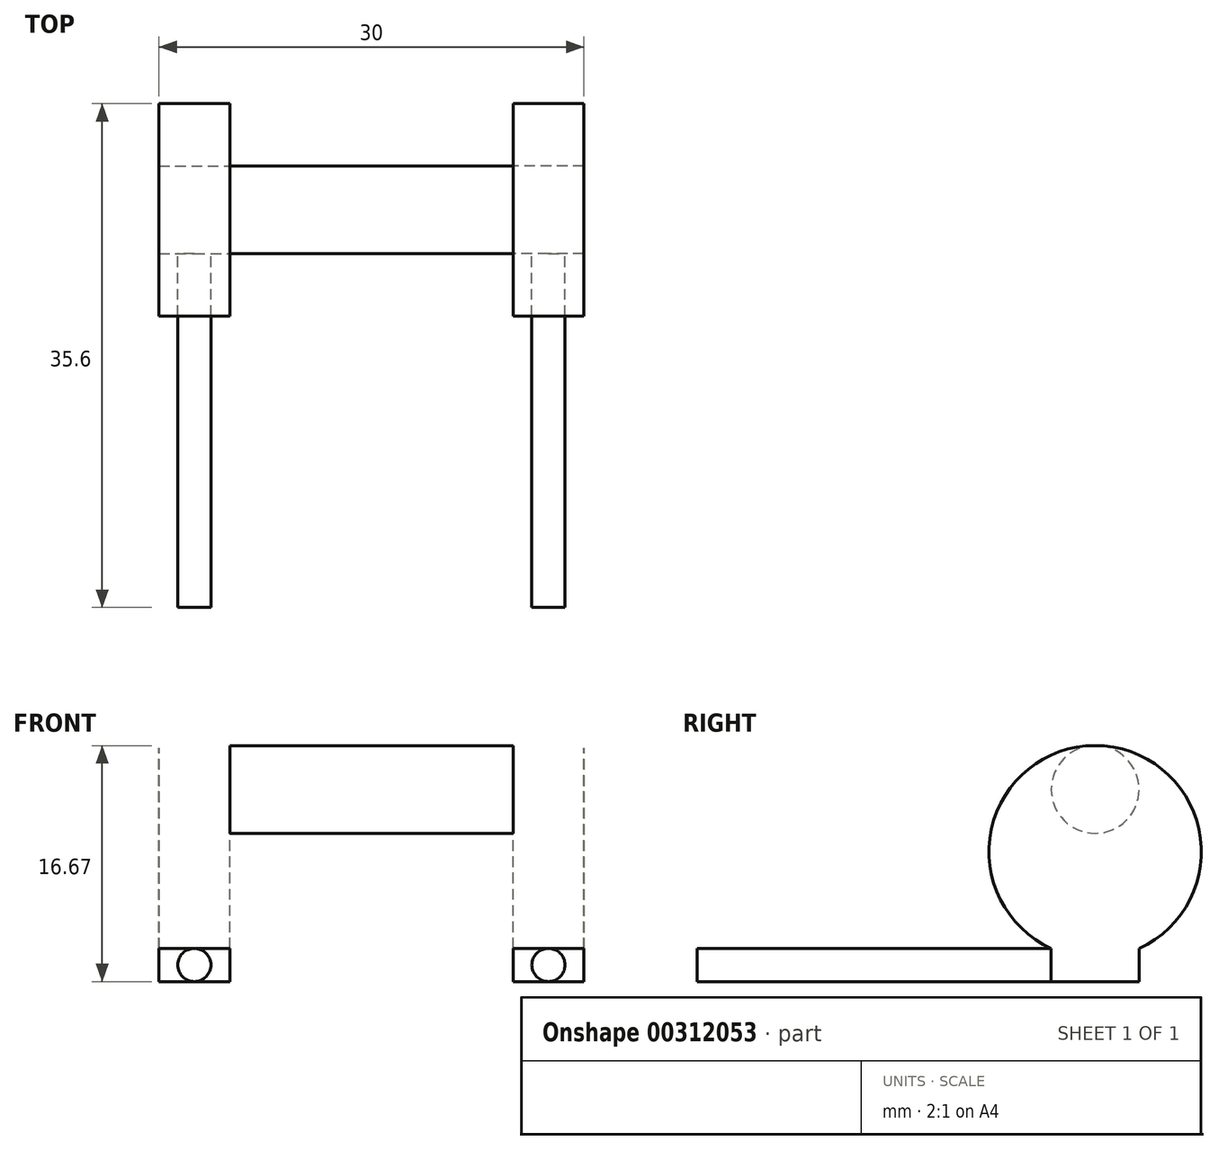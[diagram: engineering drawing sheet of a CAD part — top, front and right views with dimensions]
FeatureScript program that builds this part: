
annotation { "Feature Type Name" : "Feature", "Feature Type Description" : "" }
export const myFeature = defineFeature(function(context is Context, id is Id, definition is map)
    precondition{}
    {
        {
            var Q0;
            Q0=qCreatedBy(makeId("Right.planeOp"),FACE);
            var sketch = newSketch(context, id + "F0", { "sketchPlane" : qUnion([Q0])});
            skCircle(sketch, "E0", {"center": v(0, 0) * mm, "radius": 3.1 * mm});
            skSolve(sketch);
        }
        {
            var Q0;
            Q0 = qSketchRegion(id + "F0", true);
            extrude(context, id + "F1", {"entities" : qUnion([Q0]), "depth" : 10 * mm});
        }
        {
            var Q0;
            Q0=makeQuery(id+"F1.opExtrude","CAP_FACE",FACE,{"disambiguationData":[OSD([sQuery(id+"F0.wireOp",EDGE,"E0")])],"isStart":false});
            var sketch = newSketch(context, id + "F2", { "sketchPlane" : qUnion([Q0])});
            skCircle(sketch, "E1", {"center": v(0, -4.4) * mm, "radius": 7.5 * mm});
            skLineSegment(sketch, "E2.bottom", {"start": v(-3.1, 2.43) * mm, "end": v(3.1, 2.43) * mm});
            skLineSegment(sketch, "E2.top", {"start": v(-3.1, -13.57) * mm, "end": v(3.1, -13.57) * mm});
            skLineSegment(sketch, "E2.left", {"start": v(-3.1, 2.43) * mm, "end": v(-3.1, -13.57) * mm});
            skLineSegment(sketch, "E2.right", {"start": v(3.1, 2.43) * mm, "end": v(3.1, -13.57) * mm});
            skSolve(sketch);
        }
        {
            var Q0;
            Q0 = qSketchRegion(id + "F2", true);
            extrude(context, id + "F3", {"entities" : qUnion([Q0]), "operationType" : NewBodyOperationType.ADD, "depth" : 5 * mm});
        }
        {
            var Q0;
            Q0=makeQuery(id+"F3.opExtrude","SWEPT_FACE",FACE,{"disambiguationData":[OSD([sQuery(id+"F2.wireOp",EDGE,"E2.left")])]});
            var sketch = newSketch(context, id + "F4", { "sketchPlane" : qUnion([Q0])});
            skLineSegment(sketch, "E3", {"start": v(12.5, -11.23) * mm, "end": v(12.5, -13.57) * mm, "construction": true});
            skLineSegment(sketch, "E4", {"start": v(10, -12.4) * mm, "end": v(15, -12.4) * mm, "construction": true});
            skCircle(sketch, "E5", {"center": v(12.5, -12.4) * mm, "radius": 1.17 * mm});
            skSolve(sketch);
        }
        {
            var Q0;
            Q0 = qSketchRegion(id + "F4", true);
            extrude(context, id + "F5", {"entities" : qUnion([Q0]), "operationType" : NewBodyOperationType.ADD, "depth" : 25 * mm});
        }
        {
            var Q0;
            Q0=makeQuery(id+"F1.opExtrude","SWEPT_BODY",BODY,{"disambiguationData":[OSD([sQuery(id+"F0.wireOp",EDGE,"E0")])]});
            var Q1;
            Q1=makeQuery(id+"F1.opExtrude","CAP_FACE",FACE,{"disambiguationData":[OSD([sQuery(id+"F0.wireOp",EDGE,"E0")])],"isStart":true});
            mirror(context, id + "F6", {"operationType" : NewBodyOperationType.ADD, "entities" : qUnion([Q0]), "mirrorPlane" : qUnion([Q1])});
        }
    });
